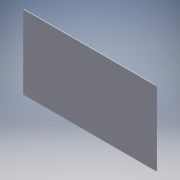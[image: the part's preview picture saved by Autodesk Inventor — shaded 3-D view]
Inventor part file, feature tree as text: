
AUTODESK INVENTOR PART (.ipt)
format: ipt  version: 2019 (Build 230136000, 136)  size: 95,232 bytes
history: native  units: mm
features: extrude x1, sketch x1
ambient origin geometry x8: Origin, YZ Plane, XZ Plane, XY Plane, X Axis, Y Axis, Z Axis, Center Point
bodies: Solid1 (feature_tree)
feature tree (2):
  extrude  "Extrusion1"  Depth=1000.0mm
  sketch  "Sketch1"  dims[d0=1800.0mm d1=1000.0mm d2=10.0mm d3=0.0mm]
